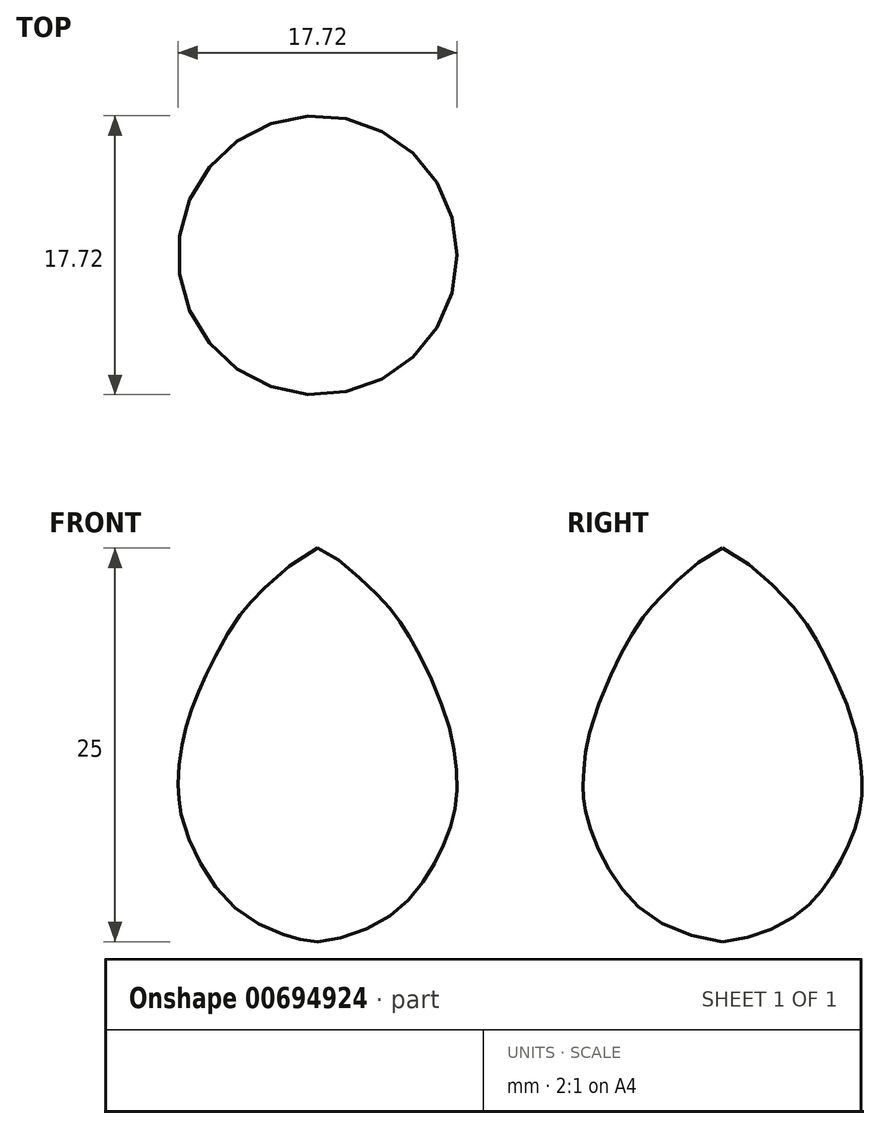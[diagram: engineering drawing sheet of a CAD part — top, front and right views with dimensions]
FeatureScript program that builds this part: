
annotation { "Feature Type Name" : "Feature", "Feature Type Description" : "" }
export const myFeature = defineFeature(function(context is Context, id is Id, definition is map)
    precondition{}
    {
        {
            var Q0;
            Q0=qCreatedBy(makeId("Front.planeOp"),FACE);
            var sketch = newSketch(context, id + "F0", { "sketchPlane" : qUnion([Q0])});
            skLineSegment(sketch, "E0", {"start": v(0, 12.5) * mm, "end": v(0, -12.5) * mm});
            skPoint(sketch, "E1", {"position": v(0, 0) * mm});
            skFitSpline(sketch, "E2", {"points": [v(0, 12.5) * mm, v(3.4, 9.93) * mm, v(5.02, 8.12) * mm, v(6.22, 6.18) * mm, v(8.04, 2.14) * mm, v(8.78, -1.16) * mm, v(8.78, -3.72) * mm, v(8.18, -5.94) * mm, v(6.83, -8.5) * mm, v(4.17, -11.15) * mm, v(0, -12.5) * mm], "startDerivative": vector(28.63, -10.6) * mm, "endDerivative": vector(-28.03, -1.42) * mm});
            skSolve(sketch);
        }
        {
            var Q0;
            Q0 = qSketchRegion(id + "F0", true);
            var Q1;
            Q1=sQuery(id+"F0.wireOp",EDGE,"E0");
            revolve(context, id + "F1", {"entities" : qUnion([Q0]), "axis" : qUnion([Q1]), "revolveType" : RevolveType.FULL});
        }
    });
